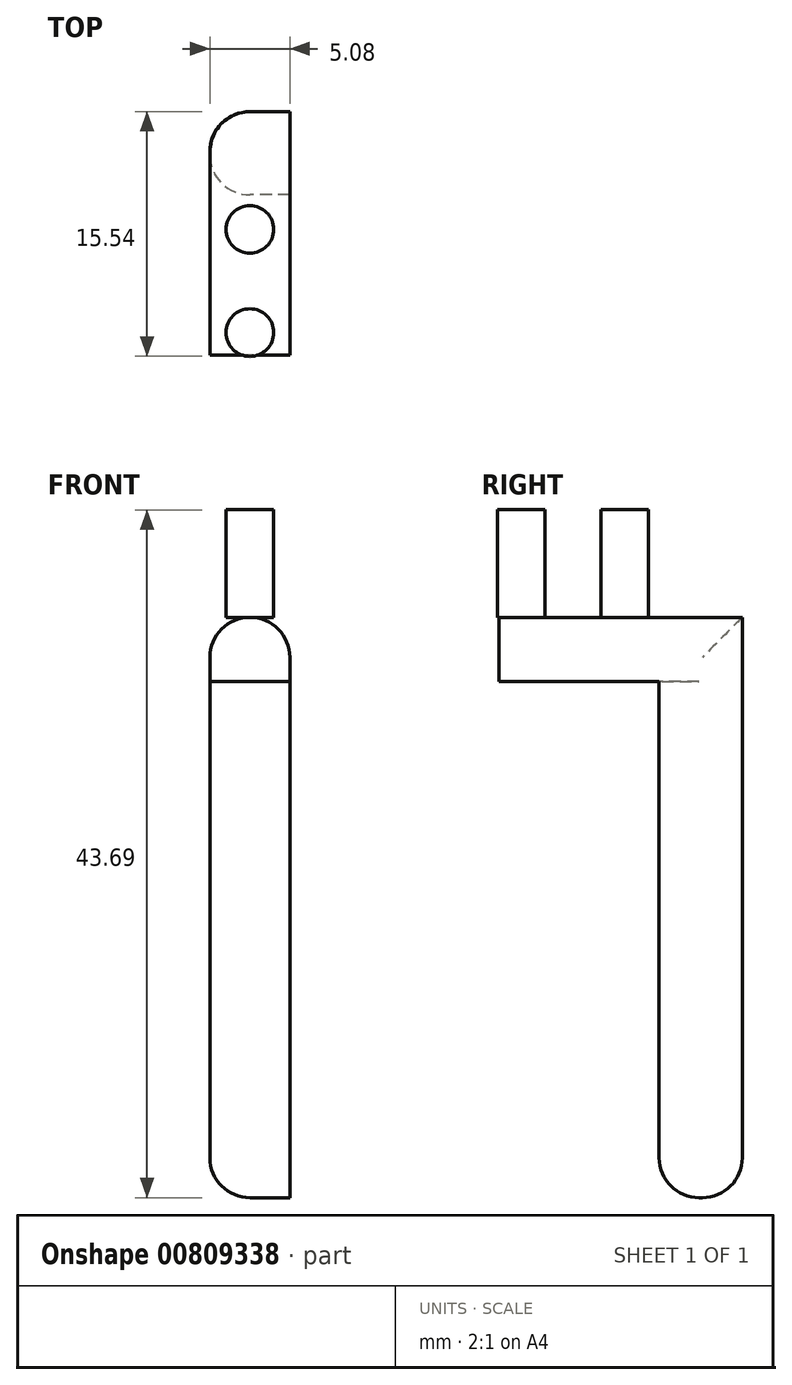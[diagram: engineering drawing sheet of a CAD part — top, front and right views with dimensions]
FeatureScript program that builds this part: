
annotation { "Feature Type Name" : "Feature", "Feature Type Description" : "" }
export const myFeature = defineFeature(function(context is Context, id is Id, definition is map)
    precondition{}
    {
        {
            var Q0;
            Q0=qCreatedBy(makeId("Top.planeOp"),FACE);
            var sketch = newSketch(context, id + "F0", { "sketchPlane" : qUnion([Q0])});
            skCircle(sketch, "E0", {"center": v(0, 6.55) * mm, "radius": 1.51 * mm});
            skCircle(sketch, "E1", {"center": v(0, 0) * mm, "radius": 1.51 * mm});
            skLineSegment(sketch, "E2", {"start": v(0, 6.55) * mm, "end": v(0, 0) * mm});
            skSolve(sketch);
        }
        {
            var Q0;
            Q0 = qSketchRegion(id + "F0", true);
            extrude(context, id + "F1", {"entities" : qUnion([Q0]), "depth" : 6.83 * mm, "offsetDistance" : 25.4 * mm});
        }
        {
            var Q0;
            Q0=qCreatedBy(makeId("Right.planeOp"),FACE);
            var sketch = newSketch(context, id + "F2", { "sketchPlane" : qUnion([Q0])});
            skLineSegment(sketch, "E3.bottom", {"start": v(-1.44, 0) * mm, "end": v(14.03, 0) * mm});
            skLineSegment(sketch, "E3.top", {"start": v(-1.44, -4.06) * mm, "end": v(14.03, -4.06) * mm});
            skLineSegment(sketch, "E3.left", {"start": v(-1.44, 0) * mm, "end": v(-1.44, -4.06) * mm});
            skLineSegment(sketch, "E3.right", {"start": v(14.03, 0) * mm, "end": v(14.03, -4.06) * mm});
            skSolve(sketch);
        }
        {
            var Q0;
            Q0=makeQuery(id+"F2.imprint","IMPRINT",FACE,{"disambiguationData":[TD([[makeQuery(id+"F2.imprint","IMPRINT",EDGE,{"derivedFrom":sQuery(id+"F2.wireOp",EDGE,"E3.bottom")}),-1.0]])]});
            extrude(context, id + "F3", {"entities" : qUnion([Q0]), "depth" : 2.54 * mm, "offsetDistance" : 25.4 * mm, "hasSecondDirection" : true, "secondDirectionOppositeDirection" : true, "secondDirectionDepth" : 2.54 * mm});
        }
        {
            var Q0;
            Q0=qCreatedBy(makeId("Right.planeOp"),FACE);
            var sketch = newSketch(context, id + "F4", { "sketchPlane" : qUnion([Q0])});
            skLineSegment(sketch, "E4.bottom", {"start": v(8.75, -4.06) * mm, "end": v(14.03, -4.06) * mm});
            skLineSegment(sketch, "E4.top", {"start": v(8.75, -36.86) * mm, "end": v(14.03, -36.86) * mm});
            skLineSegment(sketch, "E4.left", {"start": v(8.75, -4.06) * mm, "end": v(8.75, -36.86) * mm});
            skLineSegment(sketch, "E4.right", {"start": v(14.03, -4.06) * mm, "end": v(14.03, -36.86) * mm});
            skLineSegment(sketch, "E5.bottom", {"start": v(14.03, -36.86) * mm, "end": v(2.48, -36.86) * mm});
            skLineSegment(sketch, "E5.top", {"start": v(14.03, -39.63) * mm, "end": v(2.48, -39.63) * mm});
            skLineSegment(sketch, "E5.left", {"start": v(14.03, -36.86) * mm, "end": v(14.03, -39.63) * mm});
            skLineSegment(sketch, "E5.right", {"start": v(2.48, -36.86) * mm, "end": v(2.48, -39.63) * mm});
            skSolve(sketch);
        }
        {
            var Q0;
            Q0=makeQuery(id+"F4.imprint","IMPRINT",FACE,{"disambiguationData":[TD([[makeQuery(id+"F4.imprint","IMPRINT",EDGE,{"derivedFrom":sQuery(id+"F4.wireOp",EDGE,"E4.bottom")}),-1.0]])]});
            extrude(context, id + "F5", {"entities" : qUnion([Q0]), "operationType" : NewBodyOperationType.ADD, "depth" : 2.54 * mm, "offsetDistance" : 25.4 * mm, "hasSecondDirection" : true, "secondDirectionOppositeDirection" : true, "secondDirectionDepth" : 2.54 * mm});
        }
        {
            var Q0;
            Q0=makeQuery(id+"F5.opExtrude","SWEPT_EDGE",EDGE,{"disambiguationData":[OSD([sQuery(id+"F4.wireOp",EDGE,"E4.top"),sQuery(id+"F4.wireOp",EDGE,"E4.left"),sQuery(id+"F4.wireOp",EDGE,"E5.bottom")])]});
            var Q1;
            Q1=makeQuery(id+"F5.opExtrude","SWEPT_EDGE",EDGE,{"disambiguationData":[OSD([sQuery(id+"F4.wireOp",EDGE,"E4.top"),sQuery(id+"F4.wireOp",EDGE,"E4.right"),sQuery(id+"F4.wireOp",EDGE,"E5.left")])]});
            fillet(context, id + "F6", {"entities" : qUnion([Q0, Q1]), "radius" : 2.54 * mm, "tangentPropagation" : true, "allowEdgeOverflow" : false});
        }
        {
            var Q0;
            Q0=makeQuery(id+"F3.opExtrude","CAP_EDGE",EDGE,{"disambiguationData":[OSD([sQuery(id+"F2.wireOp",EDGE,"E3.bottom")])],"isStart":false});
            var Q1;
            Q1=makeQuery(id+"F3.opExtrude","CAP_EDGE",EDGE,{"disambiguationData":[OSD([sQuery(id+"F2.wireOp",EDGE,"E3.bottom")])],"isStart":true});
            var Q2;
            Q2=makeQuery(id+"F5.boolean.opBoolean","MERGE",EDGE,{"derivedFrom":[makeQuery(id+"F3.opExtrude","CAP_EDGE",EDGE,{"disambiguationData":[OSD([sQuery(id+"F2.wireOp",EDGE,"E3.right")])],"isStart":true}),makeQuery(id+"F5.opExtrude","CAP_EDGE",EDGE,{"disambiguationData":[OSD([sQuery(id+"F4.wireOp",EDGE,"E4.right")])],"isStart":true})]});
            fillet(context, id + "F7", {"entities" : qUnion([Q0, Q1, Q2]), "radius" : 2.54 * mm, "tangentPropagation" : true, "allowEdgeOverflow" : false});
        }
    });
